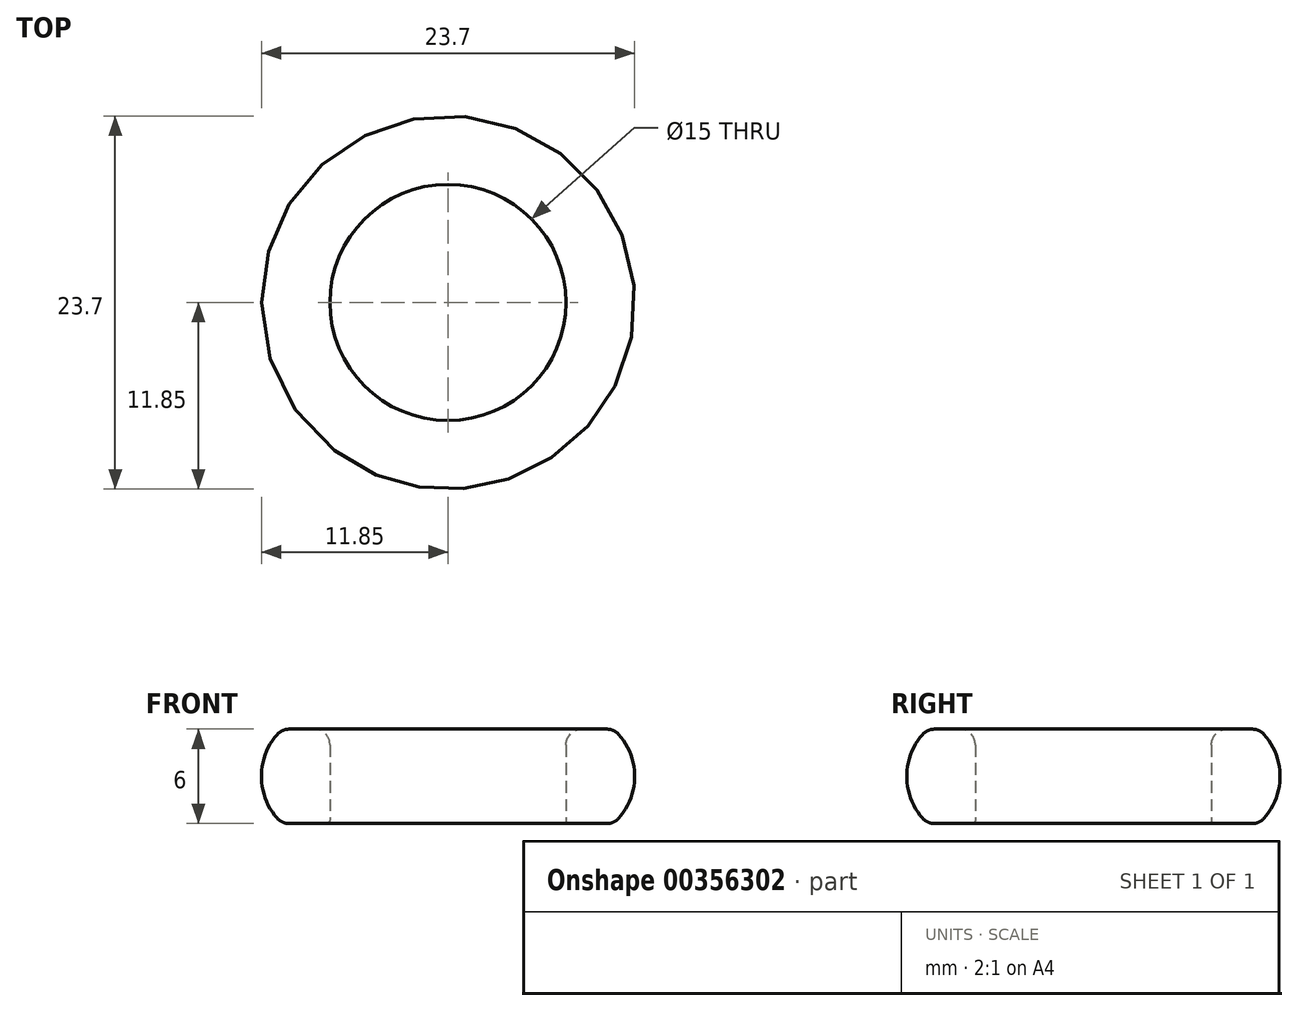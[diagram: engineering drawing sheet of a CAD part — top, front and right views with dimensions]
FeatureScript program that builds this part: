
annotation { "Feature Type Name" : "Feature", "Feature Type Description" : "" }
export const myFeature = defineFeature(function(context is Context, id is Id, definition is map)
    precondition{}
    {
        {
            var Q0;
            Q0=qCreatedBy(makeId("Front.planeOp"),FACE);
            var sketch = newSketch(context, id + "F0", { "sketchPlane" : qUnion([Q0])});
            skLineSegment(sketch, "E0", {"start": v(0, 0.2) * mm, "end": v(0, 5) * mm});
            skLineSegment(sketch, "E1", {"start": v(-2.6, 6) * mm, "end": v(-1, 6) * mm});
            skLineSegment(sketch, "E2", {"start": v(-0.2, 0) * mm, "end": v(-2.6, 0) * mm});
            skArc(sketch, "E3", {"start": v(-3.34, 5.67) * mm, "mid": v(-4.35, 3) * mm, "end": v(-3.34, 0.33) * mm});
            skPoint(sketch, "E4.visualSharp", {"position": v(-3, 6) * mm});
            skArc(sketch, "E4.filletArc", {"start": v(-2.6, 6) * mm, "mid": v(-3, 5.91) * mm, "end": v(-3.34, 5.67) * mm});
            skPoint(sketch, "E5.visualSharp", {"position": v(-3, 0) * mm});
            skArc(sketch, "E5.filletArc", {"start": v(-3.34, 0.33) * mm, "mid": v(-3, 0.09) * mm, "end": v(-2.6, 0) * mm});
            skPoint(sketch, "E6.visualSharp", {"position": v(0, 6) * mm});
            skArc(sketch, "E6.filletArc", {"start": v(0, 5) * mm, "mid": v(-0.3, 5.7) * mm, "end": v(-1, 6) * mm});
            skPoint(sketch, "E7.visualSharp", {"position": v(0, 0) * mm});
            skArc(sketch, "E7.filletArc", {"start": v(-0.2, 0) * mm, "mid": v(-0.06, 0.06) * mm, "end": v(0, 0.2) * mm});
            skLineSegment(sketch, "E8.0", {"start": v(7.5, 0.2) * mm, "end": v(7.5, 5) * mm});
            skSolve(sketch);
        }
        {
            var Q0;
            Q0=makeQuery(id+"F0.imprint","IMPRINT",FACE,{"disambiguationData":[TD([[makeQuery(id+"F0.imprint","IMPRINT",EDGE,{"derivedFrom":sQuery(id+"F0.wireOp",EDGE,"E0")}),1.0]])]});
            var Q1;
            Q1=sQuery(id+"F0.wireOp",EDGE,"E8.0");
            revolve(context, id + "F1", {"entities" : qUnion([Q0]), "axis" : qUnion([Q1]), "revolveType" : RevolveType.FULL});
        }
    });
